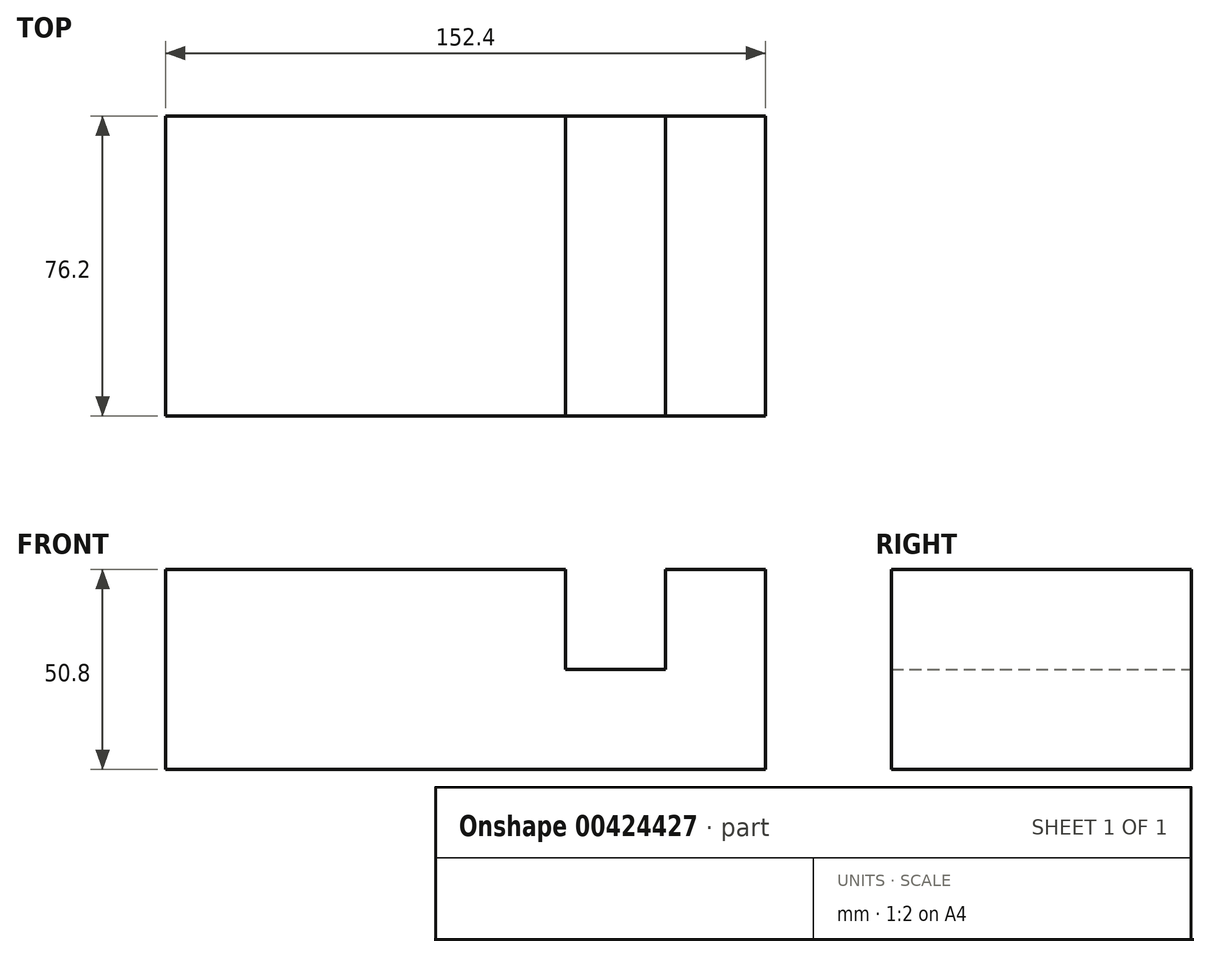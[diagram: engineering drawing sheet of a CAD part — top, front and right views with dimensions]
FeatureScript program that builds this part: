
annotation { "Feature Type Name" : "Feature", "Feature Type Description" : "" }
export const myFeature = defineFeature(function(context is Context, id is Id, definition is map)
    precondition{}
    {
        {
            var Q0;
            Q0=qCreatedBy(makeId("Front.planeOp"),FACE);
            var sketch = newSketch(context, id + "F0", { "sketchPlane" : qUnion([Q0])});
            skLineSegment(sketch, "E0", {"start": v(0, 0) * mm, "end": v(152.4, 0) * mm});
            skLineSegment(sketch, "E1", {"start": v(152.4, 0) * mm, "end": v(152.4, 50.8) * mm});
            skLineSegment(sketch, "E2", {"start": v(152.4, 50.8) * mm, "end": v(127, 50.8) * mm});
            skLineSegment(sketch, "E3", {"start": v(127, 50.8) * mm, "end": v(127, 25.4) * mm});
            skLineSegment(sketch, "E4", {"start": v(127, 25.4) * mm, "end": v(101.6, 25.4) * mm});
            skLineSegment(sketch, "E5", {"start": v(101.6, 25.4) * mm, "end": v(101.6, 50.8) * mm});
            skLineSegment(sketch, "E6", {"start": v(101.6, 50.8) * mm, "end": v(0, 50.8) * mm});
            skLineSegment(sketch, "E7", {"start": v(0, 50.8) * mm, "end": v(0, 0) * mm});
            skSolve(sketch);
        }
        {
            var Q0;
            Q0 = qSketchRegion(id + "F0", true);
            extrude(context, id + "F1", {"entities" : qUnion([Q0]), "depth" : 76.2 * mm});
        }
    });
